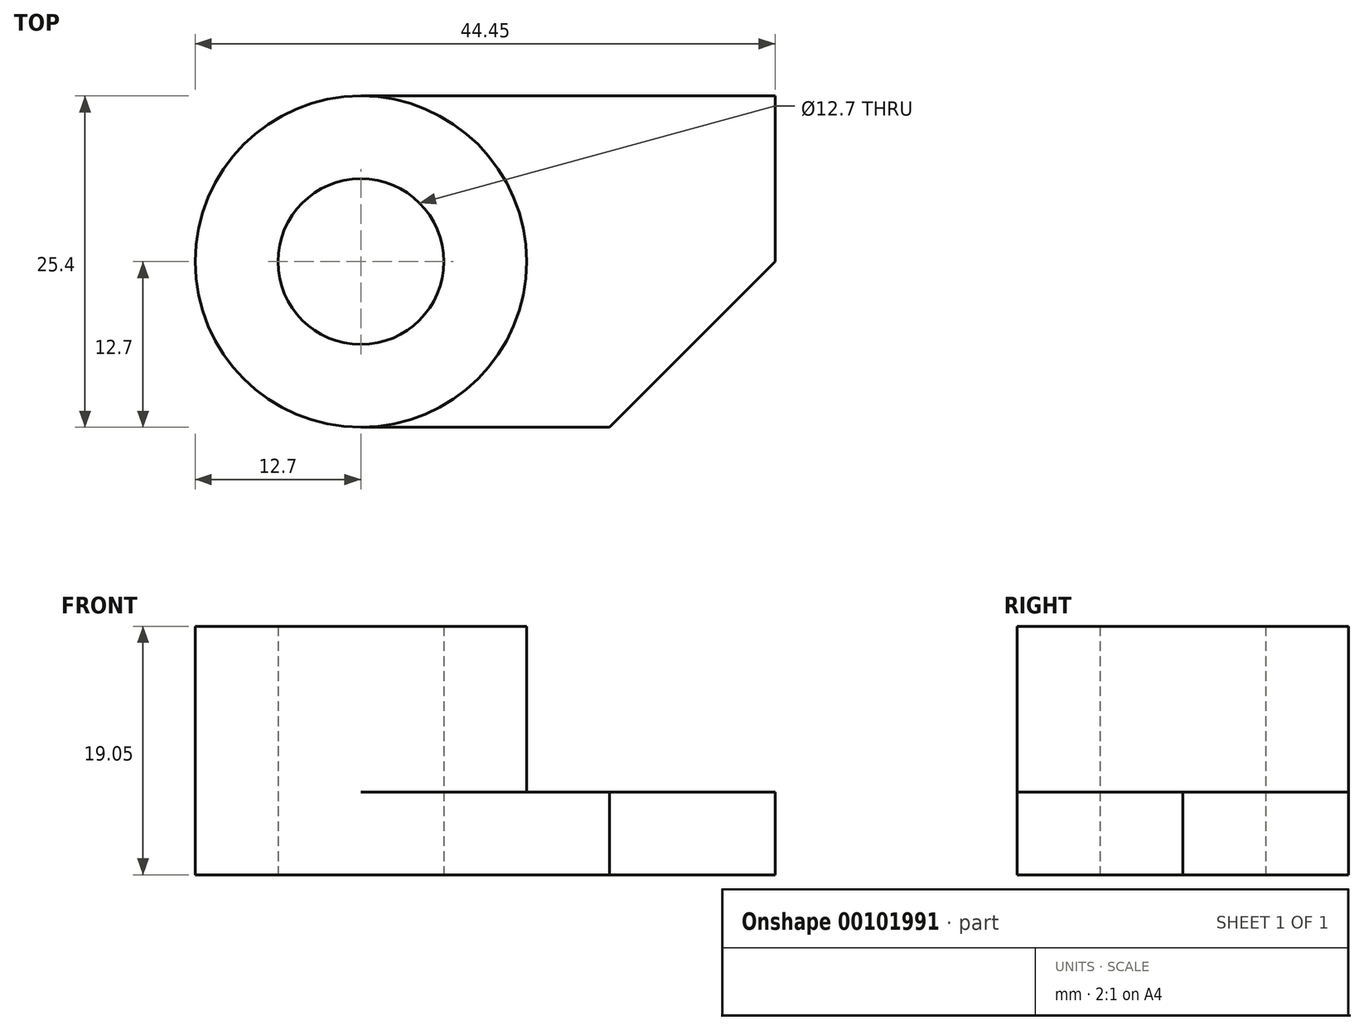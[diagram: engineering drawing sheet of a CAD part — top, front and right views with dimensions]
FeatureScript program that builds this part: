
annotation { "Feature Type Name" : "Feature", "Feature Type Description" : "" }
export const myFeature = defineFeature(function(context is Context, id is Id, definition is map)
    precondition{}
    {
        {
            var Q0;
            Q0=qCreatedBy(makeId("Top.planeOp"),FACE);
            var sketch = newSketch(context, id + "F0", { "sketchPlane" : qUnion([Q0])});
            skLineSegment(sketch, "E0", {"start": v(19.05, 0) * mm, "end": v(19.05, 12.7) * mm});
            skLineSegment(sketch, "E1", {"start": v(19.05, 0) * mm, "end": v(6.35, 0) * mm, "construction": true});
            skLineSegment(sketch, "E2", {"start": v(6.35, 0) * mm, "end": v(6.35, -12.7) * mm, "construction": true});
            skLineSegment(sketch, "E3", {"start": v(6.35, -12.7) * mm, "end": v(19.05, 0) * mm});
            skCircle(sketch, "E4", {"center": v(-12.7, 0) * mm, "radius": 6.35 * mm});
            skLineSegment(sketch, "E5", {"start": v(-12.7, 12.7) * mm, "end": v(19.05, 12.7) * mm});
            skLineSegment(sketch, "E6", {"start": v(-12.7, -12.7) * mm, "end": v(6.35, -12.7) * mm});
            skCircle(sketch, "E7", {"center": v(-12.7, 0) * mm, "radius": 12.7 * mm});
            skSolve(sketch);
        }
        {
            var Q0;
            Q0=makeQuery(id+"F0.imprint","IMPRINT",FACE,{"disambiguationData":[TD([[makeQuery(id+"F0.imprint","IMPRINT",EDGE,{"derivedFrom":sQuery(id+"F0.wireOp",EDGE,"E4")}),-1.0]])]});
            extrude(context, id + "F1", {"entities" : qUnion([Q0]), "depth" : 19.05 * mm});
        }
        {
            var Q0;
            Q0=makeQuery(id+"F0.imprint","IMPRINT",FACE,{"disambiguationData":[TD([[makeQuery(id+"F0.imprint","IMPRINT",EDGE,{"derivedFrom":sQuery(id+"F0.wireOp",EDGE,"E0")}),1.0]])]});
            extrude(context, id + "F2", {"entities" : qUnion([Q0]), "operationType" : NewBodyOperationType.ADD, "depth" : 6.35 * mm});
        }
    });
